# Revit family: Reece_Tap_Sussex_Scala_Horizontal_Sink Mixer_Pullout
name_source: partatom
category: Plumbing Fixtures
revit_build: Autodesk Revit 2018 (Build: 20180329_1100(x64)
units: mm (PartAtom-declared; Revit-internal decimal feet)

## family parameters
Cut with Voids When Loaded = No
Host = Face
Part Type = Normal
Room Calculation Point = Yes
Round Connector Dimension = Use Diameter
Shared = Yes

## types (1)
- 235 mm_5 Star_Chrome
    CWFU = 0
    Default Elevation = 1000 mm  [stored 3.28084 ft]
    Description = Scala Horizontal Pullout Sink Mixer Tap 2 Functions Chrome (5 Star)
    Disclaimer = THIS FILE IS THE PROPERTY OF THE REECE GROUP. IT MAY NOT BE REPRODUCED, REVERSE-ENGINEERED OR MODIFIED. ANY REPUBLICATION, TRANSMISSION OR DISTRIBUTION FOR THE PURPOSE OF COMMERCIALLY EXPLOITING THE FILES IS PROHIBITED.
    HWFU = 0
    Keynote = Product #2263090, Reece_Tap_Sussex_Scala_Horizontal_Sink Mixer_Pullout - 235 mm_5 Star_Chrome
    Manufacturer = Sussex
    Model = Scala
    Reece_Detail_Additional = Pullout
    Reece_Detail_Disclaimer = THIS FILE IS THE PROPERTY OF THE REECE GROUP. IT MAY NOT BE REPRODUCED, REVERSE-ENGINEERED OR MODIFIED. ANY REPUBLICATION, TRANSMISSION OR DISTRIBUTION FOR THE PURPOSE OF COMMERCIALLY EXPLOITING THE FILES IS PROHIBITED.
    Reece_Detail_Shape = Horizontal
    Reece_Detail_Type = Sink Mixer
    Reece_Material_Main = Reece_Brass_Chrome
    Reece_Material_Secondary = Reece_Plastic_Black
    Reece_Overall_Diameter = 54 mm
    Reece_Overall_Height = 265 mm
    Reece_Product_Brand = Sussex
    Reece_Product_Description = Sussex Scala Horizontal Pullout Sink Mixer Tap 2 Functions Chrome (5 Star)
    Reece_Product_Mount = Hob Mounted
    Reece_Product_Number = 2263090
    Reece_Product_Sub Brand = Scala
    Reece_Product_Type = Tap
    Reece_Product_Web Page = https://www.reece.com.au
    Reece_Tap_Clearance = 225 mm
    Reece_Tap_Inlet = 12 mm  [stored 0.0393701 ft]
    Reece_Tap_Reach = 235 mm
    Type Comments = Tap
    URL = https://www.reece.com.au
    WFU = 0

note: [stored X ft] marks values corroborated as IEEE doubles in the binary element streams (Revit-internal decimal feet)

## geometry (parser evidence)
native form markers: Sweep x3
no freeform markers — native parametric forms only
